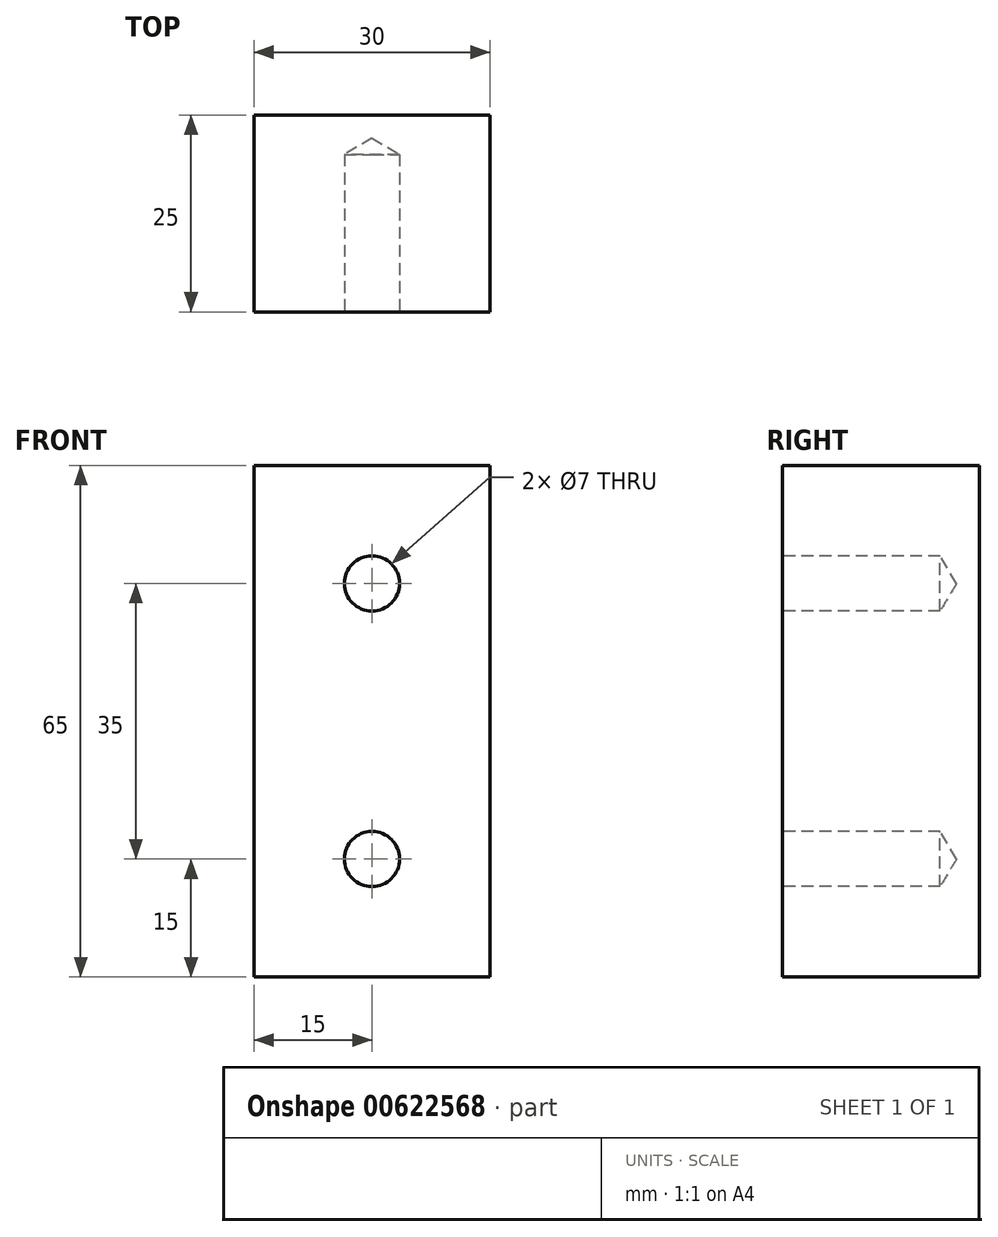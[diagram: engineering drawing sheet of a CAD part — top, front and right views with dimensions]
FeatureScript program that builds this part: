
annotation { "Feature Type Name" : "Feature", "Feature Type Description" : "" }
export const myFeature = defineFeature(function(context is Context, id is Id, definition is map)
    precondition{}
    {
        {
            var Q0;
            Q0=qCreatedBy(makeId("Top.planeOp"),FACE);
            var sketch = newSketch(context, id + "F0", { "sketchPlane" : qUnion([Q0])});
            skLineSegment(sketch, "E0.bottom", {"start": v(15, 12.5) * mm, "end": v(-15, 12.5) * mm});
            skLineSegment(sketch, "E0.top", {"start": v(15, -12.5) * mm, "end": v(-15, -12.5) * mm});
            skLineSegment(sketch, "E0.left", {"start": v(15, 12.5) * mm, "end": v(15, -12.5) * mm});
            skLineSegment(sketch, "E0.right", {"start": v(-15, 12.5) * mm, "end": v(-15, -12.5) * mm});
            skPoint(sketch, "E0.middle", {"position": v(0, 0) * mm});
            skSolve(sketch);
        }
        {
            var Q0;
            Q0=makeQuery(id+"F0.imprint","IMPRINT",FACE,{"disambiguationData":[TD([[makeQuery(id+"F0.imprint","IMPRINT",EDGE,{"derivedFrom":sQuery(id+"F0.wireOp",EDGE,"E0.bottom")}),1.0]])]});
            extrude(context, id + "F1", {"entities" : qUnion([Q0]), "oppositeDirection" : true, "depth" : 65 * mm, "offsetDistance" : 25 * mm});
        }
        {
            var Q0;
            Q0=makeQuery(id+"F1.opExtrude","SWEPT_FACE",FACE,{"disambiguationData":[OSD([sQuery(id+"F0.wireOp",EDGE,"E0.top")])]});
            var sketch = newSketch(context, id + "F2", { "sketchPlane" : qUnion([Q0])});
            skLineSegment(sketch, "E1", {"start": v(-24.52, -15) * mm, "end": v(28.96, -15) * mm, "construction": true});
            skLineSegment(sketch, "E2", {"start": v(-24.84, -50) * mm, "end": v(32.37, -50) * mm, "construction": true});
            skLineSegment(sketch, "E3", {"start": v(0, 6.62) * mm, "end": v(0, -65.94) * mm, "construction": true});
            skCircle(sketch, "E4", {"center": v(0, -15) * mm, "radius": 4 * mm});
            skCircle(sketch, "E5", {"center": v(0, -50) * mm, "radius": 4 * mm});
            skSolve(sketch);
        }
        {
            var Q0;
            Q0=sQuery(id+"F2.wireOp",VERTEX,"E4.center");
            var Q1;
            Q1=sQuery(id+"F2.wireOp",VERTEX,"E5.center");
            var Q2;
            Q2=makeQuery(id+"F1.opExtrude","SWEPT_BODY",BODY,{"disambiguationData":[OSD([sQuery(id+"F0.wireOp",EDGE,"E0.bottom"),sQuery(id+"F0.wireOp",EDGE,"E0.top"),sQuery(id+"F0.wireOp",EDGE,"E0.left"),sQuery(id+"F0.wireOp",EDGE,"E0.right")])]});
            hole(context, id + "F3", {"style" : HoleStyle.SIMPLE, "endStyle" : HoleEndStyle.BLIND, "standardTappedOrClearance" : lookupTablePath({ "standard" : "ISO", "engagement" : "75%", "pitch" : "1 mm", "size" : "M8", "type" : "Tapped" }), "standardBlindInLast" : lookupTablePath({ "standard" : "ISO", "engagement" : "75%", "pitch" : "1 mm", "size" : "M8", "type" : "Tapped" }), "holeDiameter" : 7 * mm, "majorDiameter" : 8 * mm, "showTappedDepth" : true, "holeDepth" : 20 * mm, "isTappedThrough" : true, "tappedDepth" : 20 * mm, "tapClearance" : 0, "startFromSketch" : true, "locations" : qUnion([Q0, Q1]), "scope" : qUnion([Q2])});
        }
    });
